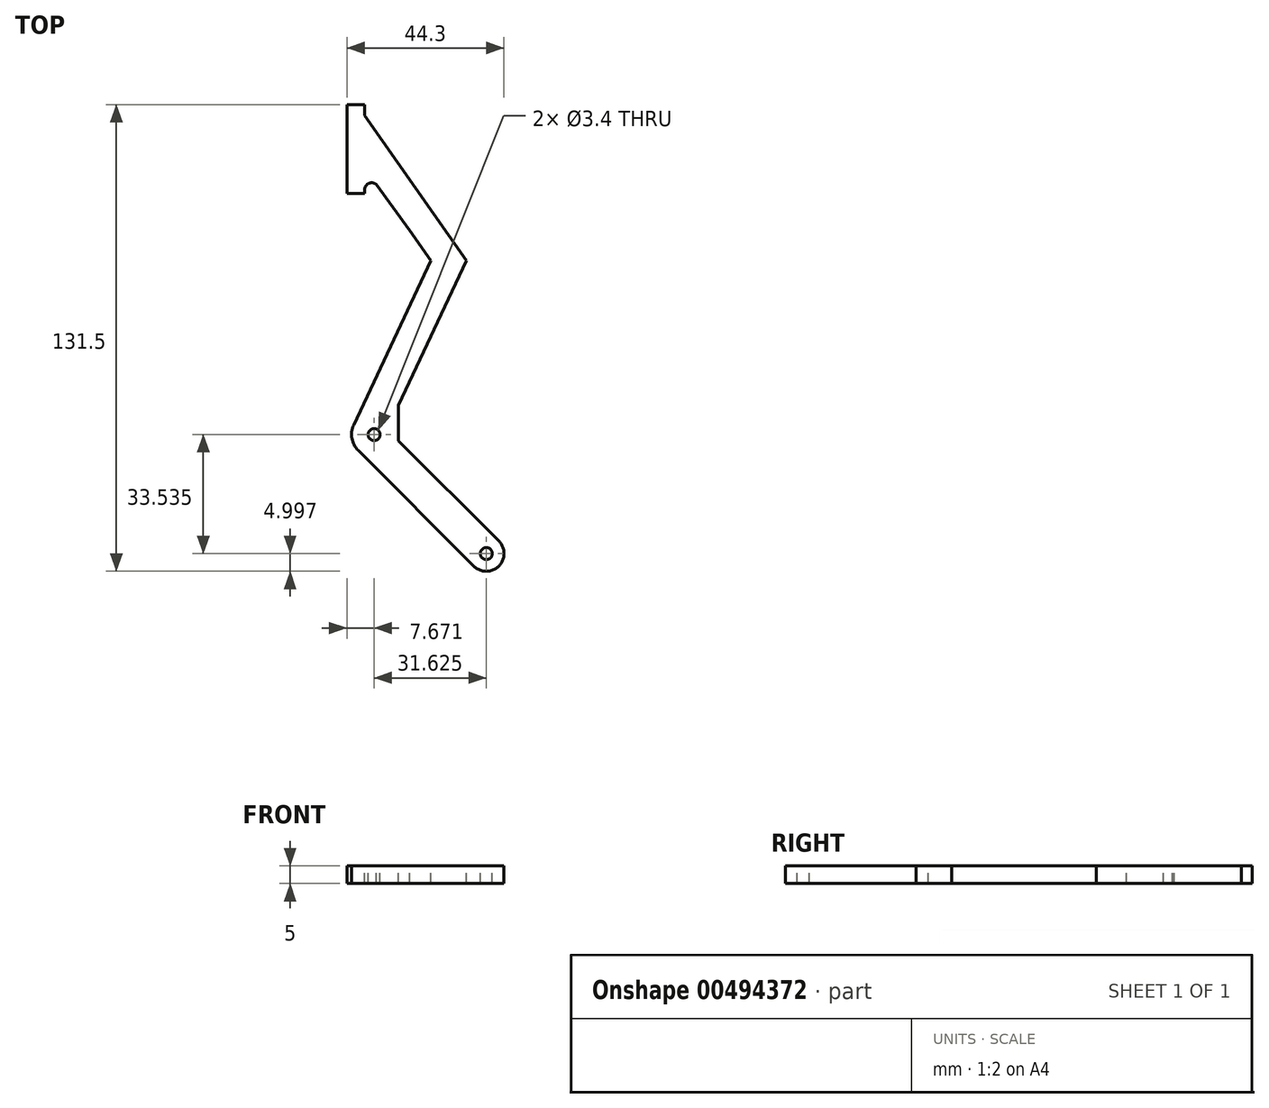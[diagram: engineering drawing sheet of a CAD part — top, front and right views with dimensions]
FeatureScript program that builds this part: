
annotation { "Feature Type Name" : "Feature", "Feature Type Description" : "" }
export const myFeature = defineFeature(function(context is Context, id is Id, definition is map)
    precondition{}
    {
        {
            var Q0;
            Q0=qCreatedBy(makeId("Top.planeOp"),FACE);
            var sketch = newSketch(context, id + "F0", { "sketchPlane" : qUnion([Q0])});
            skLineSegment(sketch, "E0", {"start": v(9.55, 67.67) * mm, "end": v(14.55, 67.67) * mm});
            skLineSegment(sketch, "E1", {"start": v(14.55, 67.67) * mm, "end": v(14.55, 42.67) * mm});
            skLineSegment(sketch, "E2", {"start": v(14.55, 42.67) * mm, "end": v(9.55, 42.67) * mm});
            skLineSegment(sketch, "E3", {"start": v(9.55, 67.67) * mm, "end": v(9.55, 64.67) * mm});
            skLineSegment(sketch, "E4", {"start": v(9.55, 42.67) * mm, "end": v(9.55, 43.67) * mm});
            skLineSegment(sketch, "E5", {"start": v(9.55, 64.67) * mm, "end": v(-19.12, 23.72) * mm});
            skLineSegment(sketch, "E6", {"start": v(-19.12, 23.72) * mm, "end": v(0.01, -17.01) * mm});
            skLineSegment(sketch, "E7", {"start": v(-9.12, 23.72) * mm, "end": v(12.63, -22.6) * mm});
            skLineSegment(sketch, "E8", {"start": v(0.01, -17.01) * mm, "end": v(0.01, -27.01) * mm});
            skLineSegment(sketch, "E9", {"start": v(0.01, -27.01) * mm, "end": v(-28.27, -55.3) * mm});
            skLineSegment(sketch, "E10", {"start": v(-9.12, 23.72) * mm, "end": v(-3.12, 32.3) * mm});
            skArc(sketch, "E11", {"start": v(9.55, 43.67) * mm, "mid": v(8.39, 45.5) * mm, "end": v(6.24, 45.19) * mm});
            skLineSegment(sketch, "E12", {"start": v(-3.12, 32.3) * mm, "end": v(6.24, 45.19) * mm});
            skLineSegment(sketch, "E13", {"start": v(0.01, -27.01) * mm, "end": v(7.08, -34.08) * mm});
            skLineSegment(sketch, "E14", {"start": v(7.08, -34.08) * mm, "end": v(11.38, -29.79) * mm});
            skPoint(sketch, "E15.newPointA", {"position": v(16.39, -30.59) * mm});
            skArc(sketch, "E15.filletArc", {"start": v(11.38, -29.79) * mm, "mid": v(13.14, -26.4) * mm, "end": v(12.63, -22.6) * mm});
            skCircle(sketch, "E16", {"center": v(6.89, -25.3) * mm, "radius": 1.7 * mm});
            skLineSegment(sketch, "E17", {"start": v(7.08, -34.08) * mm, "end": v(-21.2, -62.37) * mm});
            skLineSegment(sketch, "E18", {"start": v(-21.2, -62.37) * mm, "end": v(-28.27, -55.3) * mm});
            skArc(sketch, "E19", {"start": v(-28.27, -55.3) * mm, "mid": v(-28.27, -62.37) * mm, "end": v(-21.2, -62.37) * mm});
            skCircle(sketch, "E20", {"center": v(-24.74, -58.83) * mm, "radius": 1.7 * mm});
            skSolve(sketch);
        }
        {
            var Q0;
            Q0 = qSketchRegion(id + "F0", true);
            extrude(context, id + "F1", {"entities" : qUnion([Q0]), "depth" : 5 * mm});
        }
        {
            var Q0;
            Q0=makeQuery(id+"F1.opExtrude","SWEPT_BODY",BODY,{"disambiguationData":[OSD([sQuery(id+"F0.wireOp",EDGE,"E0"),sQuery(id+"F0.wireOp",EDGE,"E1"),sQuery(id+"F0.wireOp",EDGE,"E2"),sQuery(id+"F0.wireOp",EDGE,"E3"),sQuery(id+"F0.wireOp",EDGE,"E4"),sQuery(id+"F0.wireOp",EDGE,"E5"),sQuery(id+"F0.wireOp",EDGE,"E6"),sQuery(id+"F0.wireOp",EDGE,"E7"),sQuery(id+"F0.wireOp",EDGE,"E8"),sQuery(id+"F0.wireOp",EDGE,"E9"),sQuery(id+"F0.wireOp",EDGE,"E10"),sQuery(id+"F0.wireOp",EDGE,"E11"),sQuery(id+"F0.wireOp",EDGE,"E12"),sQuery(id+"F0.wireOp",EDGE,"E14"),sQuery(id+"F0.wireOp",EDGE,"E15.filletArc"),sQuery(id+"F0.wireOp",EDGE,"E16"),sQuery(id+"F0.wireOp",EDGE,"E17"),sQuery(id+"F0.wireOp",EDGE,"E19"),sQuery(id+"F0.wireOp",EDGE,"E20")])]});
            var Q1;
            Q1=makeQuery(id+"F1.opExtrude","CAP_EDGE",EDGE,{"disambiguationData":[OSD([sQuery(id+"F0.wireOp",EDGE,"E1")])],"isStart":false});
            transform(context, id + "F2", {"entities" : qUnion([Q0]), "transformType" : TransformType.ROTATION, "transformAxis" : qUnion([Q1]), "angle" : 180 * degree, "makeCopy" : false});
        }
        {
            var Q0;
            Q0=makeQuery(id+"F1.opExtrude","SWEPT_BODY",BODY,{"disambiguationData":[OSD([sQuery(id+"F0.wireOp",EDGE,"E0"),sQuery(id+"F0.wireOp",EDGE,"E1"),sQuery(id+"F0.wireOp",EDGE,"E2"),sQuery(id+"F0.wireOp",EDGE,"E3"),sQuery(id+"F0.wireOp",EDGE,"E4"),sQuery(id+"F0.wireOp",EDGE,"E5"),sQuery(id+"F0.wireOp",EDGE,"E6"),sQuery(id+"F0.wireOp",EDGE,"E7"),sQuery(id+"F0.wireOp",EDGE,"E8"),sQuery(id+"F0.wireOp",EDGE,"E9"),sQuery(id+"F0.wireOp",EDGE,"E10"),sQuery(id+"F0.wireOp",EDGE,"E11"),sQuery(id+"F0.wireOp",EDGE,"E12"),sQuery(id+"F0.wireOp",EDGE,"E14"),sQuery(id+"F0.wireOp",EDGE,"E15.filletArc"),sQuery(id+"F0.wireOp",EDGE,"E16"),sQuery(id+"F0.wireOp",EDGE,"E17"),sQuery(id+"F0.wireOp",EDGE,"E19"),sQuery(id+"F0.wireOp",EDGE,"E20")])]});
            transform(context, id + "F3", {"entities" : qUnion([Q0]), "transformType" : TransformType.TRANSLATION_3D, "dx" : 7.62 * mm, "dy" : 0 * mm, "dz" : 0 * mm, "makeCopy" : false});
        }
    });
